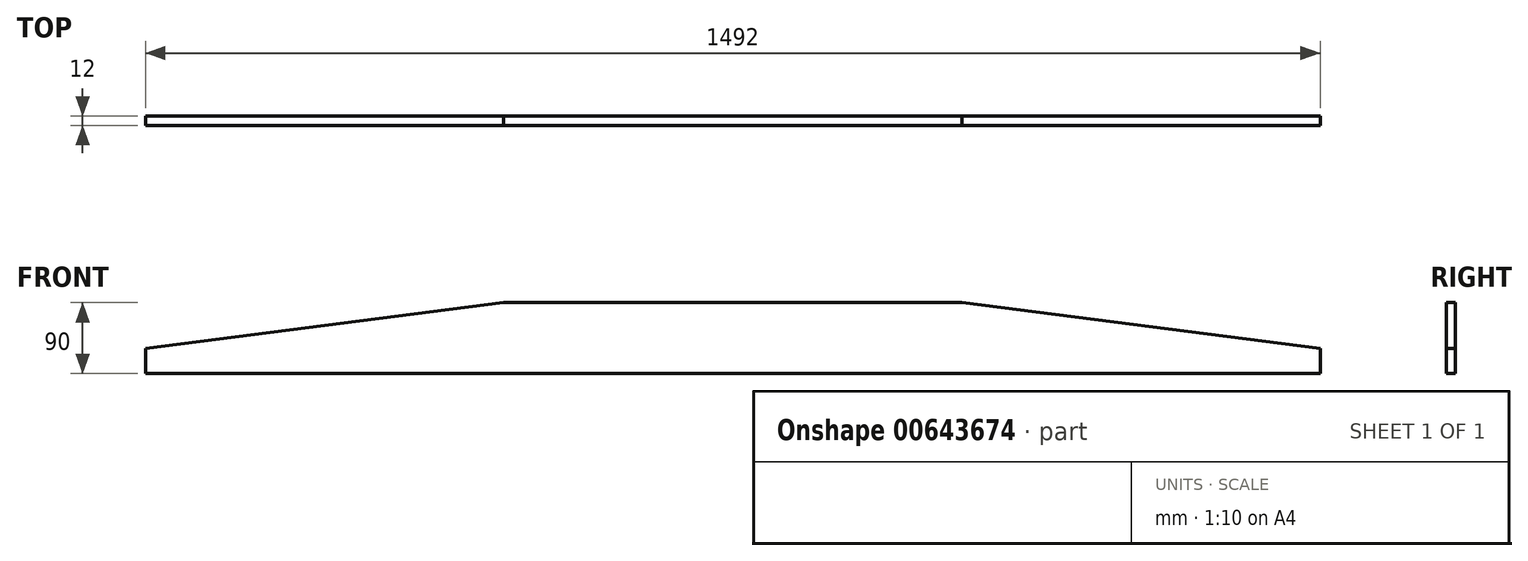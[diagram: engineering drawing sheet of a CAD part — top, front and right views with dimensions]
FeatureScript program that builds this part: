
annotation { "Feature Type Name" : "Feature", "Feature Type Description" : "" }
export const myFeature = defineFeature(function(context is Context, id is Id, definition is map)
    precondition{}
    {
        {
            var Q0;
            Q0=qCreatedBy(makeId("Front.planeOp"),FACE);
            var sketch = newSketch(context, id + "F0", { "sketchPlane" : qUnion([Q0])});
            skLineSegment(sketch, "E0.bottom", {"start": v(746, 0) * mm, "end": v(-746, 0) * mm});
            skLineSegment(sketch, "E0.top", {"start": v(291.03, 90) * mm, "end": v(-291.04, 90) * mm});
            skLineSegment(sketch, "E0.left", {"start": v(746, 0) * mm, "end": v(746, 32) * mm});
            skLineSegment(sketch, "E0.right", {"start": v(-746, 0) * mm, "end": v(-746, 32) * mm});
            skPoint(sketch, "E0.middle", {"position": v(0, 45) * mm});
            skLineSegment(sketch, "E1", {"start": v(-746, 32) * mm, "end": v(-291.04, 90) * mm});
            skLineSegment(sketch, "E2", {"start": v(746, 32) * mm, "end": v(291.03, 90) * mm});
            skPoint(sketch, "E3.orphan", {"position": v(-746, 90) * mm});
            skPoint(sketch, "E4.orphan", {"position": v(746, 90) * mm});
            skSolve(sketch);
        }
        {
            var Q0;
            Q0 = qSketchRegion(id + "F0", true);
            extrude(context, id + "F1", {"entities" : qUnion([Q0]), "depth" : 12 * mm, "offsetDistance" : 25 * mm});
        }
    });
